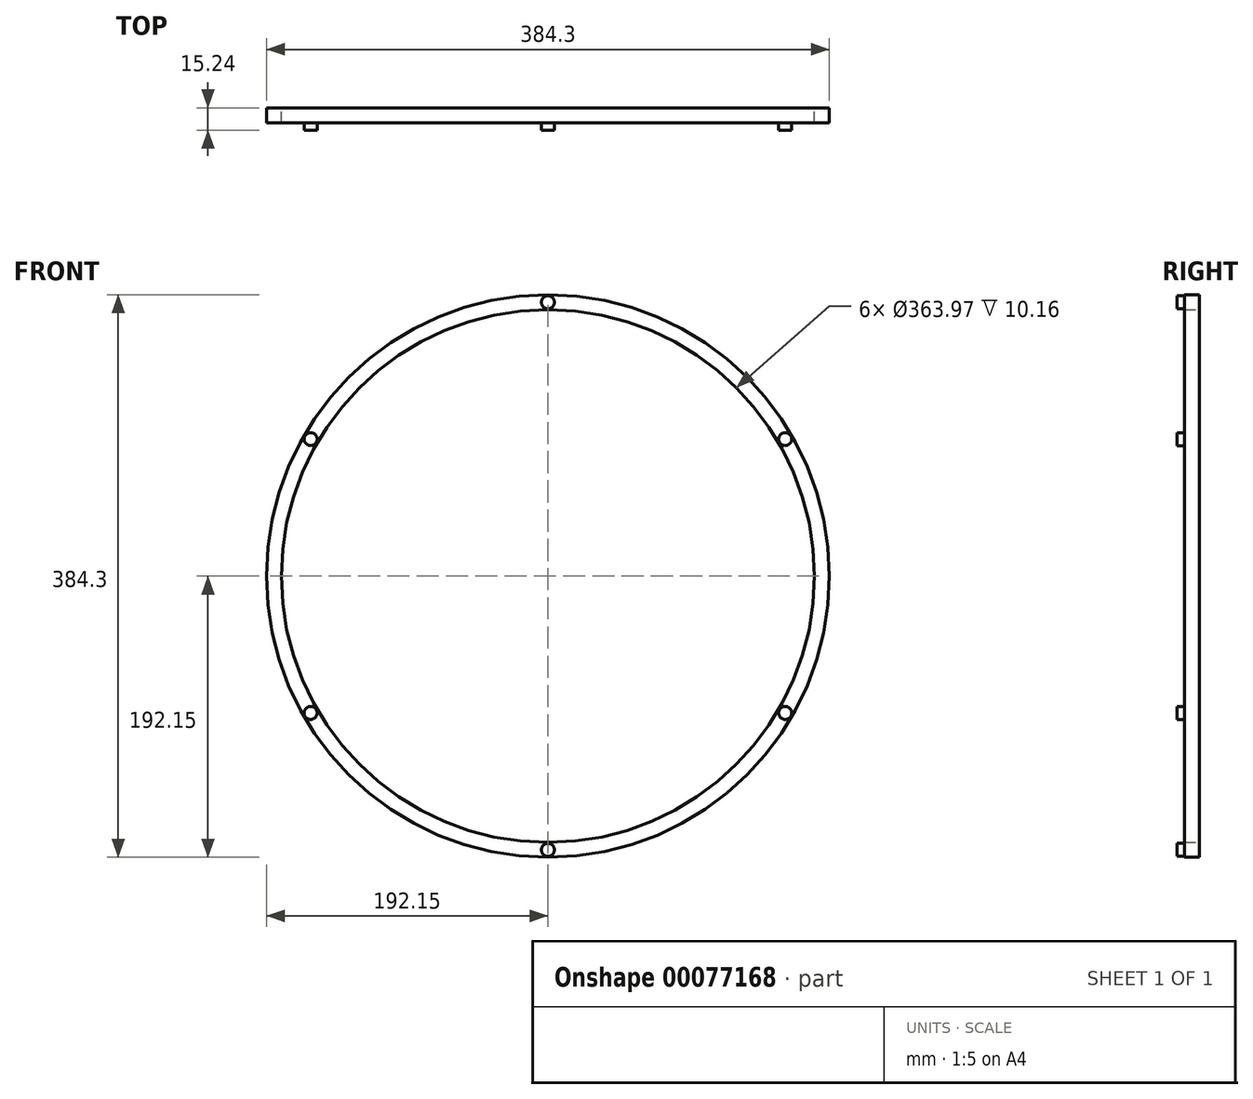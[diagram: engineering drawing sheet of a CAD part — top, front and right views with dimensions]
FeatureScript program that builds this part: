
annotation { "Feature Type Name" : "Feature", "Feature Type Description" : "" }
export const myFeature = defineFeature(function(context is Context, id is Id, definition is map)
    precondition{}
    {
        {
            var Q0;
            Q0=qCreatedBy(makeId("Front.planeOp"),FACE);
            var sketch = newSketch(context, id + "F0", { "sketchPlane" : qUnion([Q0])});
            skCircle(sketch, "E0", {"center": v(0, 0) * mm, "radius": 181.99 * mm});
            skCircle(sketch, "E1", {"center": v(0, 0) * mm, "radius": 192.15 * mm});
            skSolve(sketch);
        }
        {
            var Q0;
            Q0=makeQuery(id+"F0.imprint","IMPRINT",FACE,{"disambiguationData":[TD([[makeQuery(id+"F0.imprint","IMPRINT",EDGE,{"derivedFrom":sQuery(id+"F0.wireOp",EDGE,"E0")}),-1.0]])]});
            extrude(context, id + "F1", {"entities" : qUnion([Q0]), "depth" : 10.16 * mm});
        }
        {
            var Q0;
            Q0=makeQuery(id+"F1.opExtrude","CAP_FACE",FACE,{"disambiguationData":[OSD([sQuery(id+"F0.wireOp",EDGE,"E0"),sQuery(id+"F0.wireOp",EDGE,"E1")])],"isStart":false});
            var sketch = newSketch(context, id + "F2", { "sketchPlane" : qUnion([Q0])});
            skLineSegment(sketch, "E2", {"start": v(0, 192.15) * mm, "end": v(0, 181.99) * mm});
            skCircle(sketch, "E3", {"center": v(0, 187.06) * mm, "radius": 4.45 * mm});
            skSolve(sketch);
        }
        {
            var Q0;
            {var subQ0=sQuery(id+"F2.wireOp",EDGE,"E3");var subQ1=sQuery(id+"F2.wireOp",EDGE,"E2");var subQ2=makeQuery(id+"F2.imprint","INTERSECT",VERTEX,{"disambiguationData":[OD(0.0)],"derivedFrom":[subQ1,subQ0]});Q0=makeQuery(id+"F2.imprint","IMPRINT",FACE,{"disambiguationData":[TD([[makeQuery(id+"F2.imprint","IMPRINT",EDGE,{"disambiguationData":[TD([[subQ2,1.0]])],"derivedFrom":subQ1}),-1.0]])]});}
            var Q1;
            {var subQ0=sQuery(id+"F2.wireOp",EDGE,"E3");var subQ1=sQuery(id+"F2.wireOp",EDGE,"E2");var subQ2=makeQuery(id+"F2.imprint","INTERSECT",VERTEX,{"disambiguationData":[OD(0.0)],"derivedFrom":[subQ1,subQ0]});Q1=makeQuery(id+"F2.imprint","IMPRINT",FACE,{"disambiguationData":[TD([[makeQuery(id+"F2.imprint","IMPRINT",EDGE,{"disambiguationData":[TD([[subQ2,1.0]])],"derivedFrom":subQ1}),1.0]])]});}
            extrude(context, id + "F3", {"entities" : qUnion([Q0, Q1]), "operationType" : NewBodyOperationType.ADD, "depth" : 5.08 * mm});
        }
        {
            var Q0;
            Q0=makeQuery(id+"F1.opExtrude","SWEPT_BODY",BODY,{"disambiguationData":[OSD([sQuery(id+"F0.wireOp",EDGE,"E0"),sQuery(id+"F0.wireOp",EDGE,"E1")])]});
            var Q1;
            Q1=makeQuery(id+"F1.opExtrude","CAP_EDGE",EDGE,{"disambiguationData":[OSD([sQuery(id+"F0.wireOp",EDGE,"E0")])],"isStart":false});
            circularPattern(context, id + "F4", {"entities" : qUnion([Q0]), "axis" : qUnion([Q1]), "angle" : 60 * degree, "instanceCount" : 6});
        }
    });
